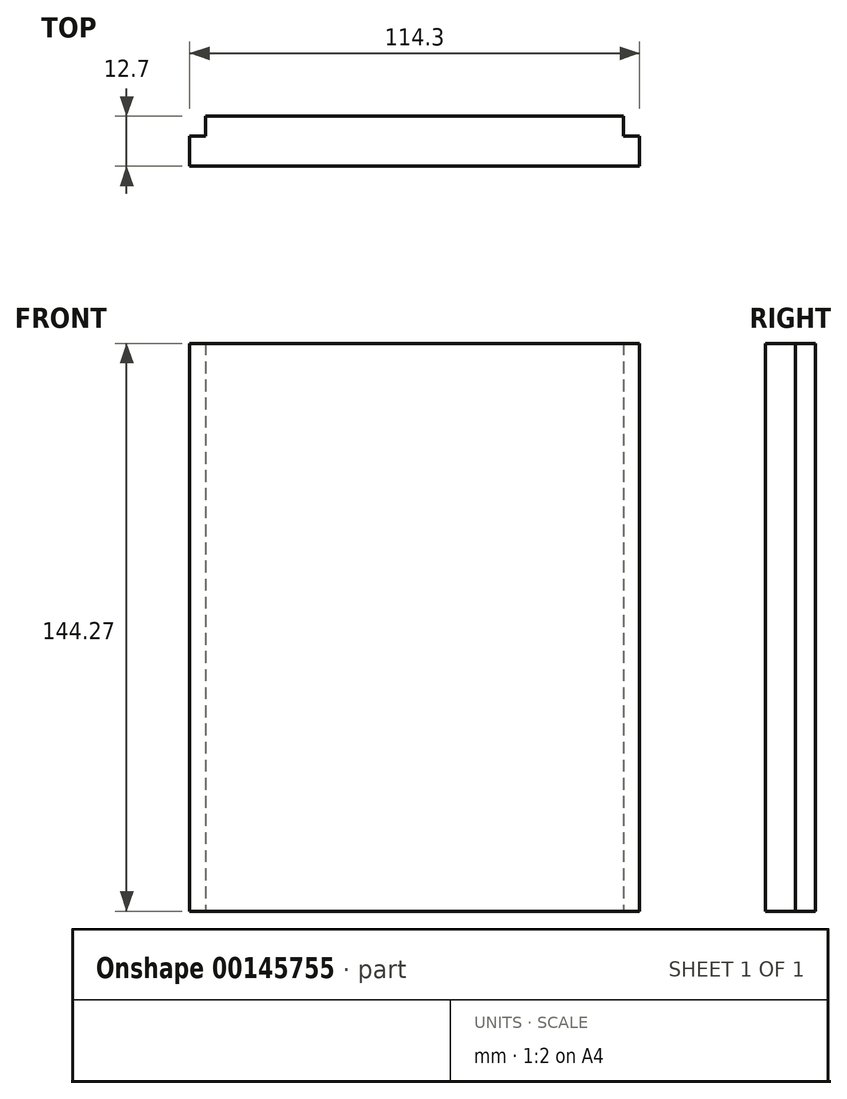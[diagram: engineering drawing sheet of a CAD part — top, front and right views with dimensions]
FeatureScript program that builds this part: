
annotation { "Feature Type Name" : "Feature", "Feature Type Description" : "" }
export const myFeature = defineFeature(function(context is Context, id is Id, definition is map)
    precondition{}
    {
        {
            var Q0;
            Q0=qCreatedBy(makeId("Top.planeOp"),FACE);
            var sketch = newSketch(context, id + "F0", { "sketchPlane" : qUnion([Q0])});
            skLineSegment(sketch, "E0.bottom", {"start": v(-36.1, 39.27) * mm, "end": v(78.2, 39.27) * mm});
            skLineSegment(sketch, "E0.top", {"start": v(-36.1, 31.65) * mm, "end": v(78.2, 31.65) * mm});
            skLineSegment(sketch, "E0.left", {"start": v(-36.1, 39.27) * mm, "end": v(-36.1, 31.65) * mm});
            skLineSegment(sketch, "E0.right", {"start": v(78.2, 39.27) * mm, "end": v(78.2, 31.65) * mm});
            skLineSegment(sketch, "E1", {"start": v(22.33, 39.27) * mm, "end": v(22.33, 39.27) * mm});
            skLineSegment(sketch, "E2.bottom", {"start": v(-32.03, 39.27) * mm, "end": v(74.14, 39.27) * mm});
            skLineSegment(sketch, "E2.top", {"start": v(-32.03, 44.35) * mm, "end": v(74.14, 44.35) * mm});
            skLineSegment(sketch, "E2.left", {"start": v(-32.03, 39.27) * mm, "end": v(-32.03, 44.35) * mm});
            skLineSegment(sketch, "E2.right", {"start": v(74.14, 39.27) * mm, "end": v(74.14, 44.35) * mm});
            skLineSegment(sketch, "E3.bottom", {"start": v(78.2, 39.27) * mm, "end": v(78.2, 39.27) * mm});
            skSolve(sketch);
        }
        {
            var Q0;
            Q0 = qSketchRegion(id + "F0", true);
            extrude(context, id + "F1", {"entities" : qUnion([Q0]), "depth" : 144.27 * mm});
        }
    });
